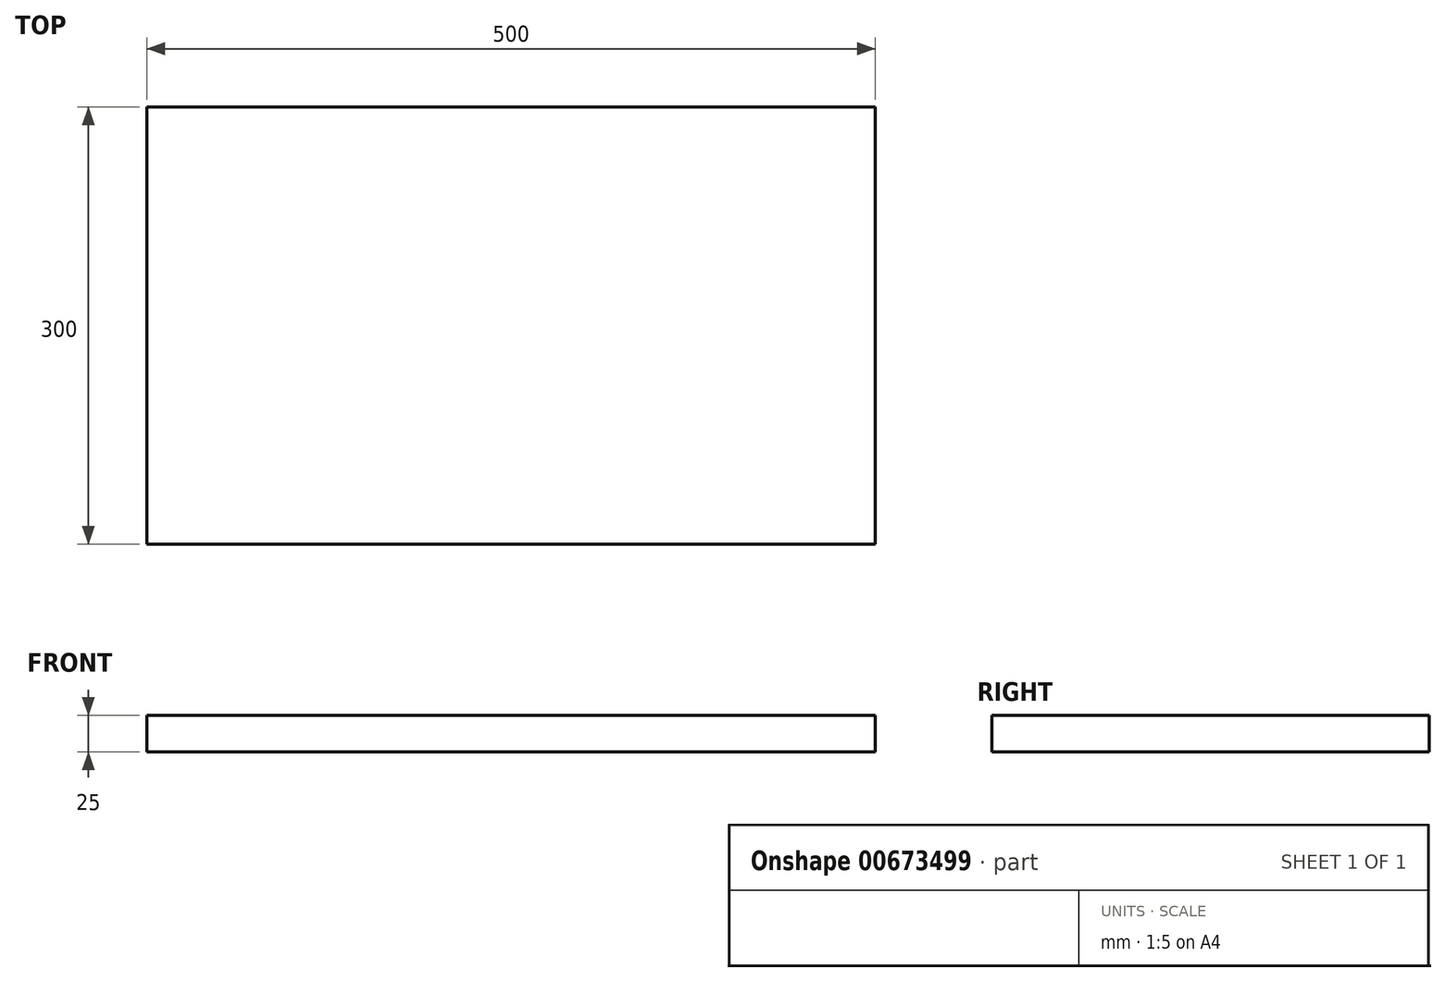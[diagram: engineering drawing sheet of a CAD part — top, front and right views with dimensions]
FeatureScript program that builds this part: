
annotation { "Feature Type Name" : "Feature", "Feature Type Description" : "" }
export const myFeature = defineFeature(function(context is Context, id is Id, definition is map)
    precondition{}
    {
        {
            var Q0;
            Q0=qCreatedBy(makeId("Top.planeOp"),FACE);
            var sketch = newSketch(context, id + "F0", { "sketchPlane" : qUnion([Q0])});
            skLineSegment(sketch, "E0.bottom", {"start": v(250, -150) * mm, "end": v(-250, -150) * mm});
            skLineSegment(sketch, "E0.top", {"start": v(250, 150) * mm, "end": v(-250, 150) * mm});
            skLineSegment(sketch, "E0.left", {"start": v(250, -150) * mm, "end": v(250, 150) * mm});
            skLineSegment(sketch, "E0.right", {"start": v(-250, -150) * mm, "end": v(-250, 150) * mm});
            skPoint(sketch, "E0.middle", {"position": v(0, 0) * mm});
            skSolve(sketch);
        }
        {
            var Q0;
            Q0=makeQuery(id+"F0.imprint","IMPRINT",FACE,{"disambiguationData":[TD([[makeQuery(id+"F0.imprint","IMPRINT",EDGE,{"derivedFrom":sQuery(id+"F0.wireOp",EDGE,"E0.bottom")}),-1.0]])]});
            extrude(context, id + "F1", {"entities" : qUnion([Q0]), "depth" : 25 * mm, "offsetDistance" : 25 * mm});
        }
    });
